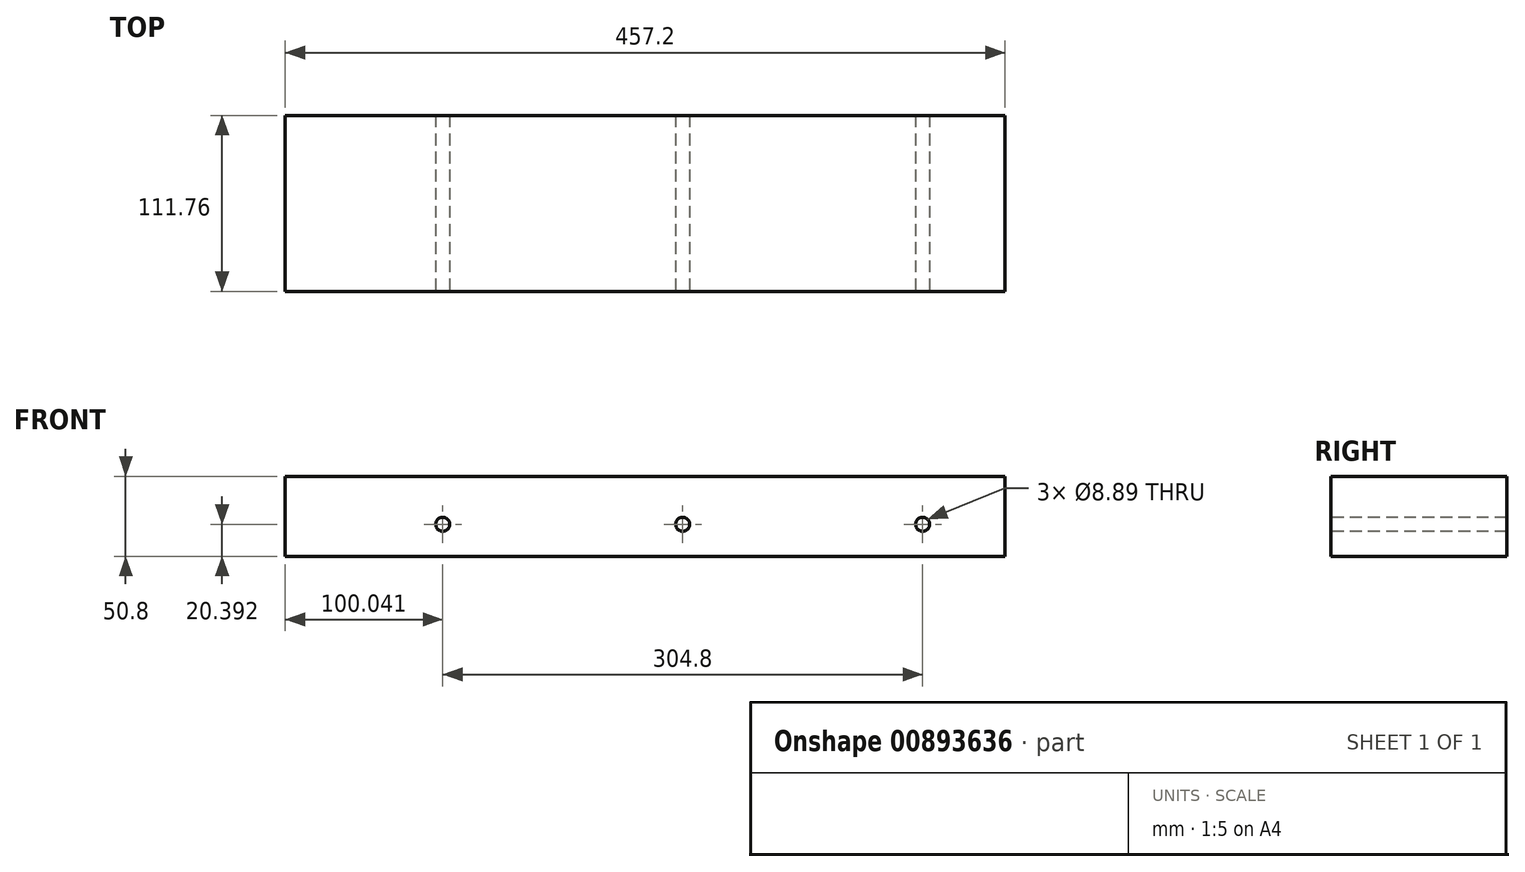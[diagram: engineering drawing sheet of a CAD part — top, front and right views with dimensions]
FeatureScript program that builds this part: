
annotation { "Feature Type Name" : "Feature", "Feature Type Description" : "" }
export const myFeature = defineFeature(function(context is Context, id is Id, definition is map)
    precondition{}
    {
        {
            var Q0;
            Q0=qCreatedBy(makeId("Front.planeOp"),FACE);
            var sketch = newSketch(context, id + "F0", { "sketchPlane" : qUnion([Q0])});
            skLineSegment(sketch, "E0.bottom", {"start": v(228.6, -25.4) * mm, "end": v(-228.6, -25.4) * mm});
            skLineSegment(sketch, "E0.top", {"start": v(228.6, 25.4) * mm, "end": v(-228.6, 25.4) * mm});
            skLineSegment(sketch, "E0.left", {"start": v(228.6, -25.4) * mm, "end": v(228.6, 25.4) * mm});
            skLineSegment(sketch, "E0.right", {"start": v(-228.6, -25.4) * mm, "end": v(-228.6, 25.4) * mm});
            skPoint(sketch, "E0.middle", {"position": v(0, 0) * mm});
            skSolve(sketch);
        }
        {
            var Q0;
            Q0=makeQuery(id+"F0.imprint","IMPRINT",FACE,{"disambiguationData":[TD([[makeQuery(id+"F0.imprint","IMPRINT",EDGE,{"derivedFrom":sQuery(id+"F0.wireOp",EDGE,"E0.bottom")}),-1.0]])]});
            extrude(context, id + "F1", {"entities" : qUnion([Q0]), "endBound" : BoundingType.SYMMETRIC, "depth" : 111.76 * mm, "offsetDistance" : 25.4 * mm});
        }
        {
            var Q0;
            Q0=makeQuery(id+"F1.opExtrude","CAP_FACE",FACE,{"disambiguationData":[OSD([sQuery(id+"F0.wireOp",EDGE,"E0.bottom"),sQuery(id+"F0.wireOp",EDGE,"E0.top"),sQuery(id+"F0.wireOp",EDGE,"E0.left"),sQuery(id+"F0.wireOp",EDGE,"E0.right")])],"isStart":false});
            var sketch = newSketch(context, id + "F2", { "sketchPlane" : qUnion([Q0])});
            skCircle(sketch, "E1", {"center": v(-128.56, -5) * mm, "radius": 4.45 * mm});
            skCircle(sketch, "E2", {"center": v(23.84, -5) * mm, "radius": 4.45 * mm});
            skCircle(sketch, "E3", {"center": v(176.24, -5) * mm, "radius": 4.45 * mm});
            skSolve(sketch);
        }
        {
            var Q0;
            Q0=makeQuery(id+"F2.imprint","IMPRINT",FACE,{"disambiguationData":[TD([[makeQuery(id+"F2.imprint","IMPRINT",EDGE,{"derivedFrom":sQuery(id+"F2.wireOp",EDGE,"E1")}),1.0]])]});
            var Q1;
            Q1=makeQuery(id+"F2.imprint","IMPRINT",FACE,{"disambiguationData":[TD([[makeQuery(id+"F2.imprint","IMPRINT",EDGE,{"derivedFrom":sQuery(id+"F2.wireOp",EDGE,"E2")}),1.0]])]});
            var Q2;
            Q2=makeQuery(id+"F2.imprint","IMPRINT",FACE,{"disambiguationData":[TD([[makeQuery(id+"F2.imprint","IMPRINT",EDGE,{"derivedFrom":sQuery(id+"F2.wireOp",EDGE,"E3")}),1.0]])]});
            var Q3;
            Q3=makeQuery(id+"F1.opExtrude","CAP_FACE",FACE,{"disambiguationData":[OSD([sQuery(id+"F0.wireOp",EDGE,"E0.bottom"),sQuery(id+"F0.wireOp",EDGE,"E0.top"),sQuery(id+"F0.wireOp",EDGE,"E0.left"),sQuery(id+"F0.wireOp",EDGE,"E0.right")])],"isStart":true});
            extrude(context, id + "F3", {"entities" : qUnion([Q0, Q1, Q2]), "operationType" : NewBodyOperationType.REMOVE, "endBound" : BoundingType.UP_TO_SURFACE, "oppositeDirection" : true, "depth" : 25.4 * mm, "endBoundEntityFace" : qUnion([Q3]), "offsetDistance" : 25.4 * mm});
        }
    });
